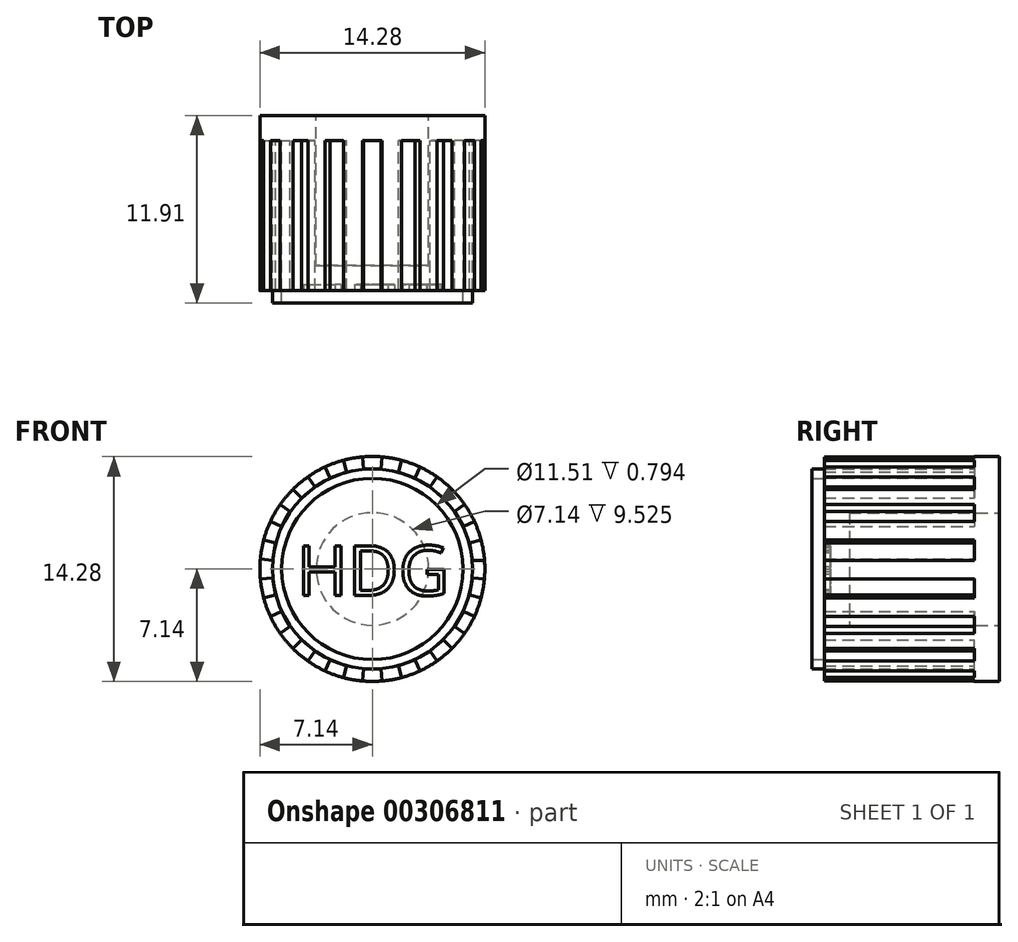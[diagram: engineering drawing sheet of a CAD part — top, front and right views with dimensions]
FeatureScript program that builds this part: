
annotation { "Feature Type Name" : "Feature", "Feature Type Description" : "" }
export const myFeature = defineFeature(function(context is Context, id is Id, definition is map)
    precondition{}
    {
        {
            var Q0;
            Q0=qCreatedBy(makeId("Front.planeOp"),FACE);
            var sketch = newSketch(context, id + "F0", { "sketchPlane" : qUnion([Q0])});
            skArc(sketch, "E0", {"start": v(-0.62, 7.12) * mm, "mid": v(-1.24, 7.04) * mm, "end": v(-1.85, 6.9) * mm});
            skLineSegment(sketch, "E1.1", {"start": v(-6.35, 0.56) * mm, "end": v(-6.16, 1.65) * mm});
            skLineSegment(sketch, "E1.3", {"start": v(-5.78, 2.7) * mm, "end": v(-5.22, 3.66) * mm});
            skLineSegment(sketch, "E1.5", {"start": v(-4.5, 4.5) * mm, "end": v(-3.66, 5.22) * mm});
            skLineSegment(sketch, "E1.7", {"start": v(-2.7, 5.78) * mm, "end": v(-1.65, 6.16) * mm});
            skLineSegment(sketch, "E1.9", {"start": v(-0.56, 6.35) * mm, "end": v(0.56, 6.35) * mm});
            skLineSegment(sketch, "E1.11", {"start": v(1.65, 6.16) * mm, "end": v(2.7, 5.78) * mm});
            skLineSegment(sketch, "E1.13", {"start": v(3.66, 5.22) * mm, "end": v(4.5, 4.5) * mm});
            skLineSegment(sketch, "E1.15", {"start": v(5.22, 3.66) * mm, "end": v(5.78, 2.7) * mm});
            skLineSegment(sketch, "E1.17", {"start": v(6.16, 1.65) * mm, "end": v(6.35, 0.56) * mm});
            skLineSegment(sketch, "E1.19", {"start": v(6.35, -0.56) * mm, "end": v(6.16, -1.65) * mm});
            skLineSegment(sketch, "E1.21", {"start": v(5.78, -2.7) * mm, "end": v(5.22, -3.66) * mm});
            skLineSegment(sketch, "E1.23", {"start": v(4.5, -4.5) * mm, "end": v(3.66, -5.22) * mm});
            skLineSegment(sketch, "E1.25", {"start": v(2.7, -5.78) * mm, "end": v(1.65, -6.16) * mm});
            skLineSegment(sketch, "E1.27", {"start": v(0.56, -6.35) * mm, "end": v(-0.56, -6.35) * mm});
            skLineSegment(sketch, "E1.29", {"start": v(-1.65, -6.16) * mm, "end": v(-2.7, -5.78) * mm});
            skLineSegment(sketch, "E1.31", {"start": v(-3.66, -5.22) * mm, "end": v(-4.5, -4.5) * mm});
            skLineSegment(sketch, "E1.33", {"start": v(-5.22, -3.66) * mm, "end": v(-5.78, -2.7) * mm});
            skLineSegment(sketch, "E1.35", {"start": v(-6.16, -1.65) * mm, "end": v(-6.35, -0.56) * mm});
            skPoint(sketch, "E1.0.midPoint", {"position": v(-6.35, 0) * mm});
            skLineSegment(sketch, "E2", {"start": v(-7.12, -0.62) * mm, "end": v(-6.35, -0.56) * mm});
            skLineSegment(sketch, "E3", {"start": v(-6.9, -1.85) * mm, "end": v(-6.16, -1.65) * mm});
            skLineSegment(sketch, "E4", {"start": v(-6.47, -3.02) * mm, "end": v(-5.78, -2.7) * mm});
            skLineSegment(sketch, "E5", {"start": v(-7.12, 0.62) * mm, "end": v(-6.35, 0.56) * mm});
            skLineSegment(sketch, "E6", {"start": v(-6.9, 1.85) * mm, "end": v(-6.16, 1.65) * mm});
            skLineSegment(sketch, "E7", {"start": v(-6.47, 3.02) * mm, "end": v(-5.78, 2.7) * mm});
            skLineSegment(sketch, "E8", {"start": v(-4.1, 5.85) * mm, "end": v(-3.66, 5.22) * mm});
            skLineSegment(sketch, "E9", {"start": v(-5.85, -4.1) * mm, "end": v(-5.22, -3.66) * mm});
            skLineSegment(sketch, "E10", {"start": v(-5.05, -5.05) * mm, "end": v(-4.5, -4.5) * mm});
            skLineSegment(sketch, "E11", {"start": v(-3.02, -6.47) * mm, "end": v(-2.7, -5.78) * mm});
            skLineSegment(sketch, "E12", {"start": v(-5.05, 5.05) * mm, "end": v(-4.5, 4.5) * mm});
            skLineSegment(sketch, "E13", {"start": v(-0.62, -7.12) * mm, "end": v(-0.56, -6.35) * mm});
            skLineSegment(sketch, "E14", {"start": v(0.62, -7.12) * mm, "end": v(0.56, -6.35) * mm});
            skLineSegment(sketch, "E15", {"start": v(4.1, -5.85) * mm, "end": v(3.66, -5.22) * mm});
            skLineSegment(sketch, "E16", {"start": v(1.85, -6.9) * mm, "end": v(1.65, -6.16) * mm});
            skLineSegment(sketch, "E17", {"start": v(3.02, -6.47) * mm, "end": v(2.7, -5.78) * mm});
            skLineSegment(sketch, "E18", {"start": v(5.05, -5.05) * mm, "end": v(4.5, -4.5) * mm});
            skLineSegment(sketch, "E19", {"start": v(-1.85, -6.9) * mm, "end": v(-1.65, -6.16) * mm});
            skLineSegment(sketch, "E20", {"start": v(6.9, -1.85) * mm, "end": v(6.16, -1.65) * mm});
            skLineSegment(sketch, "E21", {"start": v(6.9, 1.85) * mm, "end": v(6.16, 1.65) * mm});
            skLineSegment(sketch, "E22", {"start": v(6.47, 3.02) * mm, "end": v(5.78, 2.7) * mm});
            skLineSegment(sketch, "E23", {"start": v(7.12, 0.56) * mm, "end": v(6.35, 0.56) * mm});
            skLineSegment(sketch, "E24", {"start": v(7.12, -0.62) * mm, "end": v(6.35, -0.56) * mm});
            skPoint(sketch, "E24.startSnap0", {"position": v(6.25, -1.1) * mm});
            skLineSegment(sketch, "E25", {"start": v(5.85, 4.1) * mm, "end": v(5.22, 3.66) * mm});
            skLineSegment(sketch, "E26", {"start": v(5.05, 5.05) * mm, "end": v(4.5, 4.5) * mm});
            skLineSegment(sketch, "E27", {"start": v(3.02, 6.47) * mm, "end": v(2.7, 5.78) * mm});
            skPoint(sketch, "E27.startSnap0", {"position": v(3.17, 5.5) * mm});
            skLineSegment(sketch, "E28", {"start": v(1.85, 6.9) * mm, "end": v(1.65, 6.16) * mm});
            skLineSegment(sketch, "E29", {"start": v(6.47, -3.02) * mm, "end": v(5.78, -2.7) * mm});
            skLineSegment(sketch, "E30", {"start": v(0.62, 7.12) * mm, "end": v(0.56, 6.35) * mm});
            skLineSegment(sketch, "E31", {"start": v(-0.62, 7.12) * mm, "end": v(-0.56, 6.35) * mm});
            skLineSegment(sketch, "E32", {"start": v(-1.85, 6.9) * mm, "end": v(-1.65, 6.16) * mm});
            skLineSegment(sketch, "E33", {"start": v(-3.02, 6.47) * mm, "end": v(-2.7, 5.78) * mm});
            skLineSegment(sketch, "E34", {"start": v(5.85, -4.1) * mm, "end": v(5.2, -3.64) * mm});
            skLineSegment(sketch, "E35", {"start": v(4.1, 5.85) * mm, "end": v(3.66, 5.22) * mm});
            skLineSegment(sketch, "E36", {"start": v(-5.85, 4.1) * mm, "end": v(-5.2, 3.64) * mm});
            skLineSegment(sketch, "E37.trimOffspring", {"start": v(5.2, -3.64) * mm, "end": v(5.22, -3.66) * mm});
            skLineSegment(sketch, "E38.trimOffspring", {"start": v(-5.2, 3.64) * mm, "end": v(-5.22, 3.66) * mm});
            skArc(sketch, "E39.trimOffspring", {"start": v(-3.02, 6.47) * mm, "mid": v(-3.57, 6.19) * mm, "end": v(-4.1, 5.85) * mm});
            skArc(sketch, "E40.trimOffspring", {"start": v(-5.05, 5.05) * mm, "mid": v(-5.47, 4.6) * mm, "end": v(-5.85, 4.1) * mm});
            skArc(sketch, "E41.trimOffspring", {"start": v(-6.47, 3.02) * mm, "mid": v(-6.71, 2.44) * mm, "end": v(-6.9, 1.85) * mm});
            skArc(sketch, "E42.trimOffspring", {"start": v(1.85, 6.9) * mm, "mid": v(1.24, 7.04) * mm, "end": v(0.62, 7.12) * mm});
            skArc(sketch, "E43.trimOffspring", {"start": v(4.1, 5.85) * mm, "mid": v(3.57, 6.19) * mm, "end": v(3.02, 6.47) * mm});
            skArc(sketch, "E44.trimOffspring", {"start": v(5.85, 4.1) * mm, "mid": v(5.47, 4.6) * mm, "end": v(5.05, 5.05) * mm});
            skArc(sketch, "E45.trimOffspring", {"start": v(6.9, 1.85) * mm, "mid": v(6.71, 2.44) * mm, "end": v(6.47, 3.02) * mm});
            skArc(sketch, "E46.trimOffspring", {"start": v(7.12, -0.62) * mm, "mid": v(7.14, -0.03) * mm, "end": v(7.12, 0.56) * mm});
            skArc(sketch, "E47.trimOffspring", {"start": v(6.47, -3.02) * mm, "mid": v(6.71, -2.44) * mm, "end": v(6.9, -1.85) * mm});
            skArc(sketch, "E48.trimOffspring", {"start": v(5.05, -5.05) * mm, "mid": v(5.47, -4.6) * mm, "end": v(5.85, -4.1) * mm});
            skArc(sketch, "E49.trimOffspring", {"start": v(3.02, -6.47) * mm, "mid": v(3.57, -6.19) * mm, "end": v(4.1, -5.85) * mm});
            skLineSegment(sketch, "E50", {"start": v(-4.1, -5.85) * mm, "end": v(-3.66, -5.22) * mm});
            skArc(sketch, "E51.trimOffspring", {"start": v(-7.12, 0.62) * mm, "mid": v(-7.14, 0) * mm, "end": v(-7.12, -0.62) * mm});
            skArc(sketch, "E52.trimOffspring", {"start": v(-6.9, -1.85) * mm, "mid": v(-6.71, -2.44) * mm, "end": v(-6.47, -3.02) * mm});
            skArc(sketch, "E53.trimOffspring", {"start": v(-5.85, -4.1) * mm, "mid": v(-5.47, -4.6) * mm, "end": v(-5.05, -5.05) * mm});
            skArc(sketch, "E54.trimOffspring", {"start": v(-4.1, -5.85) * mm, "mid": v(-3.57, -6.19) * mm, "end": v(-3.02, -6.47) * mm});
            skArc(sketch, "E55.trimOffspring", {"start": v(-1.85, -6.9) * mm, "mid": v(-1.24, -7.04) * mm, "end": v(-0.62, -7.12) * mm});
            skArc(sketch, "E56.trimOffspring", {"start": v(0.62, -7.12) * mm, "mid": v(1.24, -7.04) * mm, "end": v(1.85, -6.9) * mm});
            skArc(sketch, "E57.trimOffspring", {"start": v(5.2, -3.64) * mm, "mid": v(5.36, -3.41) * mm, "end": v(5.5, -3.17) * mm, "construction": true});
            skSolve(sketch);
        }
        {
            var Q0;
            Q0=makeQuery(id+"F0.imprint","IMPRINT",FACE,{"disambiguationData":[TD([[makeQuery(id+"F0.imprint","IMPRINT",EDGE,{"derivedFrom":sQuery(id+"F0.wireOp",EDGE,"E0")}),1.0]])]});
            extrude(context, id + "F1", {"entities" : qUnion([Q0]), "depth" : 9.52 * mm});
        }
        {
            var Q0;
            Q0=makeQuery(id+"F1.opExtrude","CAP_FACE",FACE,{"disambiguationData":[OSD([sQuery(id+"F0.wireOp",EDGE,"E0"),sQuery(id+"F0.wireOp",EDGE,"E1.1"),sQuery(id+"F0.wireOp",EDGE,"E1.3"),sQuery(id+"F0.wireOp",EDGE,"E1.5"),sQuery(id+"F0.wireOp",EDGE,"E1.7"),sQuery(id+"F0.wireOp",EDGE,"E1.9"),sQuery(id+"F0.wireOp",EDGE,"E1.11"),sQuery(id+"F0.wireOp",EDGE,"E1.13"),sQuery(id+"F0.wireOp",EDGE,"E1.15"),sQuery(id+"F0.wireOp",EDGE,"E1.17"),sQuery(id+"F0.wireOp",EDGE,"E1.19"),sQuery(id+"F0.wireOp",EDGE,"E1.21"),sQuery(id+"F0.wireOp",EDGE,"E1.23"),sQuery(id+"F0.wireOp",EDGE,"E1.25"),sQuery(id+"F0.wireOp",EDGE,"E1.27"),sQuery(id+"F0.wireOp",EDGE,"E1.29"),sQuery(id+"F0.wireOp",EDGE,"E1.31"),sQuery(id+"F0.wireOp",EDGE,"E1.33"),sQuery(id+"F0.wireOp",EDGE,"E1.35"),sQuery(id+"F0.wireOp",EDGE,"E2"),sQuery(id+"F0.wireOp",EDGE,"E3"),sQuery(id+"F0.wireOp",EDGE,"E4"),sQuery(id+"F0.wireOp",EDGE,"E5"),sQuery(id+"F0.wireOp",EDGE,"E6"),sQuery(id+"F0.wireOp",EDGE,"E7"),sQuery(id+"F0.wireOp",EDGE,"E8"),sQuery(id+"F0.wireOp",EDGE,"E9"),sQuery(id+"F0.wireOp",EDGE,"E10"),sQuery(id+"F0.wireOp",EDGE,"E11"),sQuery(id+"F0.wireOp",EDGE,"E12"),sQuery(id+"F0.wireOp",EDGE,"E13"),sQuery(id+"F0.wireOp",EDGE,"E14"),sQuery(id+"F0.wireOp",EDGE,"E15"),sQuery(id+"F0.wireOp",EDGE,"E16"),sQuery(id+"F0.wireOp",EDGE,"E17"),sQuery(id+"F0.wireOp",EDGE,"E18"),sQuery(id+"F0.wireOp",EDGE,"E19"),sQuery(id+"F0.wireOp",EDGE,"E20"),sQuery(id+"F0.wireOp",EDGE,"E21"),sQuery(id+"F0.wireOp",EDGE,"E22"),sQuery(id+"F0.wireOp",EDGE,"E23"),sQuery(id+"F0.wireOp",EDGE,"E24"),sQuery(id+"F0.wireOp",EDGE,"E25"),sQuery(id+"F0.wireOp",EDGE,"E26"),sQuery(id+"F0.wireOp",EDGE,"E27"),sQuery(id+"F0.wireOp",EDGE,"E28"),sQuery(id+"F0.wireOp",EDGE,"E29"),sQuery(id+"F0.wireOp",EDGE,"E30"),sQuery(id+"F0.wireOp",EDGE,"E31"),sQuery(id+"F0.wireOp",EDGE,"E32"),sQuery(id+"F0.wireOp",EDGE,"E33"),sQuery(id+"F0.wireOp",EDGE,"E34"),sQuery(id+"F0.wireOp",EDGE,"E35"),sQuery(id+"F0.wireOp",EDGE,"E36"),sQuery(id+"F0.wireOp",EDGE,"E39.trimOffspring"),sQuery(id+"F0.wireOp",EDGE,"E40.trimOffspring"),sQuery(id+"F0.wireOp",EDGE,"E41.trimOffspring"),sQuery(id+"F0.wireOp",EDGE,"E42.trimOffspring"),sQuery(id+"F0.wireOp",EDGE,"E43.trimOffspring"),sQuery(id+"F0.wireOp",EDGE,"E44.trimOffspring"),sQuery(id+"F0.wireOp",EDGE,"E45.trimOffspring"),sQuery(id+"F0.wireOp",EDGE,"E46.trimOffspring"),sQuery(id+"F0.wireOp",EDGE,"E47.trimOffspring"),sQuery(id+"F0.wireOp",EDGE,"E48.trimOffspring"),sQuery(id+"F0.wireOp",EDGE,"E49.trimOffspring"),sQuery(id+"F0.wireOp",EDGE,"E50"),sQuery(id+"F0.wireOp",EDGE,"E51.trimOffspring"),sQuery(id+"F0.wireOp",EDGE,"E52.trimOffspring"),sQuery(id+"F0.wireOp",EDGE,"E53.trimOffspring"),sQuery(id+"F0.wireOp",EDGE,"E54.trimOffspring"),sQuery(id+"F0.wireOp",EDGE,"E55.trimOffspring"),sQuery(id+"F0.wireOp",EDGE,"E56.trimOffspring")])],"isStart":true});
            var sketch = newSketch(context, id + "F2", { "sketchPlane" : qUnion([Q0])});
            skCircle(sketch, "E58", {"center": v(0, 0) * mm, "radius": 7.14 * mm});
            skSolve(sketch);
        }
        {
            var Q0;
            Q0 = qSketchRegion(id + "F2", true);
            extrude(context, id + "F3", {"entities" : qUnion([Q0]), "operationType" : NewBodyOperationType.ADD, "depth" : 1.59 * mm});
        }
        {
            var Q0;
            Q0=makeQuery(id+"F1.opExtrude","CAP_FACE",FACE,{"disambiguationData":[OSD([sQuery(id+"F0.wireOp",EDGE,"E0"),sQuery(id+"F0.wireOp",EDGE,"E1.1"),sQuery(id+"F0.wireOp",EDGE,"E1.3"),sQuery(id+"F0.wireOp",EDGE,"E1.5"),sQuery(id+"F0.wireOp",EDGE,"E1.7"),sQuery(id+"F0.wireOp",EDGE,"E1.9"),sQuery(id+"F0.wireOp",EDGE,"E1.11"),sQuery(id+"F0.wireOp",EDGE,"E1.13"),sQuery(id+"F0.wireOp",EDGE,"E1.15"),sQuery(id+"F0.wireOp",EDGE,"E1.17"),sQuery(id+"F0.wireOp",EDGE,"E1.19"),sQuery(id+"F0.wireOp",EDGE,"E1.21"),sQuery(id+"F0.wireOp",EDGE,"E1.23"),sQuery(id+"F0.wireOp",EDGE,"E1.25"),sQuery(id+"F0.wireOp",EDGE,"E1.27"),sQuery(id+"F0.wireOp",EDGE,"E1.29"),sQuery(id+"F0.wireOp",EDGE,"E1.31"),sQuery(id+"F0.wireOp",EDGE,"E1.33"),sQuery(id+"F0.wireOp",EDGE,"E1.35"),sQuery(id+"F0.wireOp",EDGE,"E2"),sQuery(id+"F0.wireOp",EDGE,"E3"),sQuery(id+"F0.wireOp",EDGE,"E4"),sQuery(id+"F0.wireOp",EDGE,"E5"),sQuery(id+"F0.wireOp",EDGE,"E6"),sQuery(id+"F0.wireOp",EDGE,"E7"),sQuery(id+"F0.wireOp",EDGE,"E8"),sQuery(id+"F0.wireOp",EDGE,"E9"),sQuery(id+"F0.wireOp",EDGE,"E10"),sQuery(id+"F0.wireOp",EDGE,"E11"),sQuery(id+"F0.wireOp",EDGE,"E12"),sQuery(id+"F0.wireOp",EDGE,"E13"),sQuery(id+"F0.wireOp",EDGE,"E14"),sQuery(id+"F0.wireOp",EDGE,"E15"),sQuery(id+"F0.wireOp",EDGE,"E16"),sQuery(id+"F0.wireOp",EDGE,"E17"),sQuery(id+"F0.wireOp",EDGE,"E18"),sQuery(id+"F0.wireOp",EDGE,"E19"),sQuery(id+"F0.wireOp",EDGE,"E20"),sQuery(id+"F0.wireOp",EDGE,"E21"),sQuery(id+"F0.wireOp",EDGE,"E22"),sQuery(id+"F0.wireOp",EDGE,"E23"),sQuery(id+"F0.wireOp",EDGE,"E24"),sQuery(id+"F0.wireOp",EDGE,"E25"),sQuery(id+"F0.wireOp",EDGE,"E26"),sQuery(id+"F0.wireOp",EDGE,"E27"),sQuery(id+"F0.wireOp",EDGE,"E28"),sQuery(id+"F0.wireOp",EDGE,"E29"),sQuery(id+"F0.wireOp",EDGE,"E30"),sQuery(id+"F0.wireOp",EDGE,"E31"),sQuery(id+"F0.wireOp",EDGE,"E32"),sQuery(id+"F0.wireOp",EDGE,"E33"),sQuery(id+"F0.wireOp",EDGE,"E34"),sQuery(id+"F0.wireOp",EDGE,"E35"),sQuery(id+"F0.wireOp",EDGE,"E36"),sQuery(id+"F0.wireOp",EDGE,"E39.trimOffspring"),sQuery(id+"F0.wireOp",EDGE,"E40.trimOffspring"),sQuery(id+"F0.wireOp",EDGE,"E41.trimOffspring"),sQuery(id+"F0.wireOp",EDGE,"E42.trimOffspring"),sQuery(id+"F0.wireOp",EDGE,"E43.trimOffspring"),sQuery(id+"F0.wireOp",EDGE,"E44.trimOffspring"),sQuery(id+"F0.wireOp",EDGE,"E45.trimOffspring"),sQuery(id+"F0.wireOp",EDGE,"E46.trimOffspring"),sQuery(id+"F0.wireOp",EDGE,"E47.trimOffspring"),sQuery(id+"F0.wireOp",EDGE,"E48.trimOffspring"),sQuery(id+"F0.wireOp",EDGE,"E49.trimOffspring"),sQuery(id+"F0.wireOp",EDGE,"E50"),sQuery(id+"F0.wireOp",EDGE,"E51.trimOffspring"),sQuery(id+"F0.wireOp",EDGE,"E52.trimOffspring"),sQuery(id+"F0.wireOp",EDGE,"E53.trimOffspring"),sQuery(id+"F0.wireOp",EDGE,"E54.trimOffspring"),sQuery(id+"F0.wireOp",EDGE,"E55.trimOffspring"),sQuery(id+"F0.wireOp",EDGE,"E56.trimOffspring")])],"isStart":false});
            var sketch = newSketch(context, id + "F4", { "sketchPlane" : qUnion([Q0])});
            skCircle(sketch, "E59", {"center": v(0, 0) * mm, "radius": 6.35 * mm});
            skCircle(sketch, "E60", {"center": v(0, 0) * mm, "radius": 5.75 * mm});
            skSolve(sketch);
        }
        {
            var Q0;
            Q0=makeQuery(id+"F4.imprint","IMPRINT",FACE,{"disambiguationData":[TD([[makeQuery(id+"F4.imprint","IMPRINT",EDGE,{"derivedFrom":sQuery(id+"F4.wireOp",EDGE,"E60")}),-1.0]])]});
            extrude(context, id + "F5", {"entities" : qUnion([Q0]), "operationType" : NewBodyOperationType.ADD, "depth" : 0.8 * mm});
        }
        {
            var Q0;
            Q0=makeQuery(id+"F5.boolean.opBoolean","SPLIT",FACE,{"disambiguationData":[TD([makeQuery(id+"F5.opExtrude","SWEPT_FACE",FACE,{"disambiguationData":[OSD([sQuery(id+"F4.wireOp",EDGE,"E60")])]})])],"derivedFrom":makeQuery(id+"F1.opExtrude","CAP_FACE",FACE,{"disambiguationData":[OSD([sQuery(id+"F0.wireOp",EDGE,"E0"),sQuery(id+"F0.wireOp",EDGE,"E1.1"),sQuery(id+"F0.wireOp",EDGE,"E1.3"),sQuery(id+"F0.wireOp",EDGE,"E1.5"),sQuery(id+"F0.wireOp",EDGE,"E1.7"),sQuery(id+"F0.wireOp",EDGE,"E1.9"),sQuery(id+"F0.wireOp",EDGE,"E1.11"),sQuery(id+"F0.wireOp",EDGE,"E1.13"),sQuery(id+"F0.wireOp",EDGE,"E1.15"),sQuery(id+"F0.wireOp",EDGE,"E1.17"),sQuery(id+"F0.wireOp",EDGE,"E1.19"),sQuery(id+"F0.wireOp",EDGE,"E1.21"),sQuery(id+"F0.wireOp",EDGE,"E1.23"),sQuery(id+"F0.wireOp",EDGE,"E1.25"),sQuery(id+"F0.wireOp",EDGE,"E1.27"),sQuery(id+"F0.wireOp",EDGE,"E1.29"),sQuery(id+"F0.wireOp",EDGE,"E1.31"),sQuery(id+"F0.wireOp",EDGE,"E1.33"),sQuery(id+"F0.wireOp",EDGE,"E1.35"),sQuery(id+"F0.wireOp",EDGE,"E2"),sQuery(id+"F0.wireOp",EDGE,"E3"),sQuery(id+"F0.wireOp",EDGE,"E4"),sQuery(id+"F0.wireOp",EDGE,"E5"),sQuery(id+"F0.wireOp",EDGE,"E6"),sQuery(id+"F0.wireOp",EDGE,"E7"),sQuery(id+"F0.wireOp",EDGE,"E8"),sQuery(id+"F0.wireOp",EDGE,"E9"),sQuery(id+"F0.wireOp",EDGE,"E10"),sQuery(id+"F0.wireOp",EDGE,"E11"),sQuery(id+"F0.wireOp",EDGE,"E12"),sQuery(id+"F0.wireOp",EDGE,"E13"),sQuery(id+"F0.wireOp",EDGE,"E14"),sQuery(id+"F0.wireOp",EDGE,"E15"),sQuery(id+"F0.wireOp",EDGE,"E16"),sQuery(id+"F0.wireOp",EDGE,"E17"),sQuery(id+"F0.wireOp",EDGE,"E18"),sQuery(id+"F0.wireOp",EDGE,"E19"),sQuery(id+"F0.wireOp",EDGE,"E20"),sQuery(id+"F0.wireOp",EDGE,"E21"),sQuery(id+"F0.wireOp",EDGE,"E22"),sQuery(id+"F0.wireOp",EDGE,"E23"),sQuery(id+"F0.wireOp",EDGE,"E24"),sQuery(id+"F0.wireOp",EDGE,"E25"),sQuery(id+"F0.wireOp",EDGE,"E26"),sQuery(id+"F0.wireOp",EDGE,"E27"),sQuery(id+"F0.wireOp",EDGE,"E28"),sQuery(id+"F0.wireOp",EDGE,"E29"),sQuery(id+"F0.wireOp",EDGE,"E30"),sQuery(id+"F0.wireOp",EDGE,"E31"),sQuery(id+"F0.wireOp",EDGE,"E32"),sQuery(id+"F0.wireOp",EDGE,"E33"),sQuery(id+"F0.wireOp",EDGE,"E34"),sQuery(id+"F0.wireOp",EDGE,"E35"),sQuery(id+"F0.wireOp",EDGE,"E36"),sQuery(id+"F0.wireOp",EDGE,"E39.trimOffspring"),sQuery(id+"F0.wireOp",EDGE,"E40.trimOffspring"),sQuery(id+"F0.wireOp",EDGE,"E41.trimOffspring"),sQuery(id+"F0.wireOp",EDGE,"E42.trimOffspring"),sQuery(id+"F0.wireOp",EDGE,"E43.trimOffspring"),sQuery(id+"F0.wireOp",EDGE,"E44.trimOffspring"),sQuery(id+"F0.wireOp",EDGE,"E45.trimOffspring"),sQuery(id+"F0.wireOp",EDGE,"E46.trimOffspring"),sQuery(id+"F0.wireOp",EDGE,"E47.trimOffspring"),sQuery(id+"F0.wireOp",EDGE,"E48.trimOffspring"),sQuery(id+"F0.wireOp",EDGE,"E49.trimOffspring"),sQuery(id+"F0.wireOp",EDGE,"E50"),sQuery(id+"F0.wireOp",EDGE,"E51.trimOffspring"),sQuery(id+"F0.wireOp",EDGE,"E52.trimOffspring"),sQuery(id+"F0.wireOp",EDGE,"E53.trimOffspring"),sQuery(id+"F0.wireOp",EDGE,"E54.trimOffspring"),sQuery(id+"F0.wireOp",EDGE,"E55.trimOffspring"),sQuery(id+"F0.wireOp",EDGE,"E56.trimOffspring")])],"isStart":false})});
            var sketch = newSketch(context, id + "F6", { "sketchPlane" : qUnion([Q0])});
            skText(sketch, "E61", { "text": "HDG", "fontName": "OpenSans-Regular.ttf"});
            const initialGuessF6  = {"E61": [-0.00482, -0.00168, 1, 0, 0.00318]};
            skSetInitialGuess(sketch, initialGuessF6);
            skSolve(sketch);
        }
        {
            var Q0;
            Q0 = qSketchRegion(id + "F6", true);
            extrude(context, id + "F7", {"entities" : qUnion([Q0]), "operationType" : NewBodyOperationType.REMOVE, "oppositeDirection" : true, "depth" : 0.4 * mm});
        }
        {
            var Q0;
            Q0=makeQuery(id+"F3.opExtrude","CAP_FACE",FACE,{"disambiguationData":[OSD([sQuery(id+"F2.wireOp",EDGE,"E58")])],"isStart":false});
            var sketch = newSketch(context, id + "F8", { "sketchPlane" : qUnion([Q0])});
            skCircle(sketch, "E62", {"center": v(0, 0) * mm, "radius": 3.57 * mm});
            skSolve(sketch);
        }
        {
            var Q0;
            Q0=makeQuery(id+"F8.imprint","IMPRINT",FACE,{"disambiguationData":[TD([[makeQuery(id+"F8.imprint","IMPRINT",EDGE,{"derivedFrom":sQuery(id+"F8.wireOp",EDGE,"E62")}),1.0]])]});
            extrude(context, id + "F9", {"entities" : qUnion([Q0]), "operationType" : NewBodyOperationType.REMOVE, "oppositeDirection" : true, "depth" : 9.52 * mm});
        }
        {
            var Q0;
            Q0=qCreatedBy(makeId("Right.planeOp"),FACE);
            var sketch = newSketch(context, id + "F10", { "sketchPlane" : qUnion([Q0])});
            skCircle(sketch, "E63", {"center": v(-0.8, 0) * mm, "radius": 1.2 * mm});
            skSolve(sketch);
        }
        {
            var Q0;
            Q0 = qSketchRegion(id + "F10", true);
            extrude(context, id + "F11", {"entities" : qUnion([Q0]), "operationType" : NewBodyOperationType.REMOVE, "oppositeDirection" : true, "depth" : 1 / 50.8 * mm});
        }
    });
